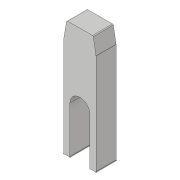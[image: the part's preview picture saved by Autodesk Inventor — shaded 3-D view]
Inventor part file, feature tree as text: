
AUTODESK INVENTOR PART (.ipt)
format: ipt  version: 2017 (Build 210142000, 142)  size: 211,456 bytes
history: native  units: in
note: dims shown in document units (in); Inventor stores cm internally (conversion verified against a paired STEP export)
features: sketch x5, extrude x3, fillet x3, projected_geometry x3, chamfer x2, sheet_metal_op x1, other x1
ambient origin geometry x8: Origin, YZ Plane, XZ Plane, XY Plane, X Axis, Y Axis, Z Axis, Center Point
bodies: Solid1 (feature_tree)
feature tree (18):
  sheet_metal_op  "Face1"
  extrude  "Extrusion1"  Depth=0.3937in
  sketch  "Sketch3"  dims[d9=0.0623in]
  extrude  "Extrusion2"  Depth=0.0623in
  chamfer  "Chamfer3"  Distance=0.125in
  chamfer  "Chamfer4"  Distance=0.125in
  fillet  "Fillet5"  Radius=1.0in
  fillet  "Fillet6"  Radius=0.0573in
  extrude  "Extrusion3"  Depth=0.002in
  fillet  "Fillet7"  Radius=0.2362in
  sketch  "Sketch1"  dims[d2=0.1969in d3=0.3937in]
  other  "Plate1"
  sketch  "Sketch2"  dims[d4=0.5512in d8=0.0623in]
  projected_geometry  "Projected Loop1"
  sketch  "Sketch4"  dims[d10=0.25in]
  projected_geometry  "Projected Loop2"
  sketch  "Sketch5"  dims[d11=0.25in d12=0.125in d14=0.125in d15=1.0in d16=0.0in d18=0.0573in d19=0.0573in d28=0.2362in d29=0.125in d30=0.2004in d31=0.1in d32=0.1in d33=0.0in d34=0.0179in d35=0.315in d36=0.0573in d37=1.0in d38=0.0in d39=0.1in d40=0.125in d41=0.0687in d42=0.1in d43=0.125in d44=0.0687in d46=0.005in d47=0.062in d48=0.005in d49=0.005in d50=0.005in d51=0.005in d52=1.0in d53=0.0in d54=0.002in]
  projected_geometry  "Projected Loop3"
